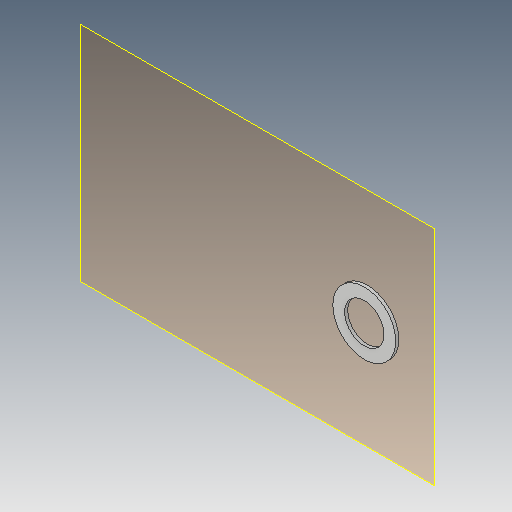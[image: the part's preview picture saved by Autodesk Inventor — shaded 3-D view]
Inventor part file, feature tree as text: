
AUTODESK INVENTOR PART (.ipt)
format: ipt  version: 2017 (Build 210142000, 142)  size: 89,088 bytes
history: native  units: mm
features: other x3, plane x1, extrude x1, sketch x1, reference x1
ambient origin geometry x8: Origin, YZ Plane, XZ Plane, XY Plane, X Axis, Y Axis, Z Axis, Center Point
bodies: Solid1 (feature_tree)
feature tree (7):
  plane  "Work Plane1"
  extrude  "Extrusion1"  [1 undecoded]
  sketch  "Sketch1"  dims[d0=0.5mm d1=0.0mm]
  reference  "Reference1"
  other  "<userpath>\OneDrive\SL-Inventor\SL-Beast 3D Printer\x-aXIS-aSSEMBLY.iam"
  other  "x-aXIS-aSSEMBLY.iam"
  other  "X-Idler:1"
note: 1 required parameter value undecoded (feature->parameter linkage not recoverable at this tier; creation-order binding heuristic only, values carry confidence <= 0.55)
